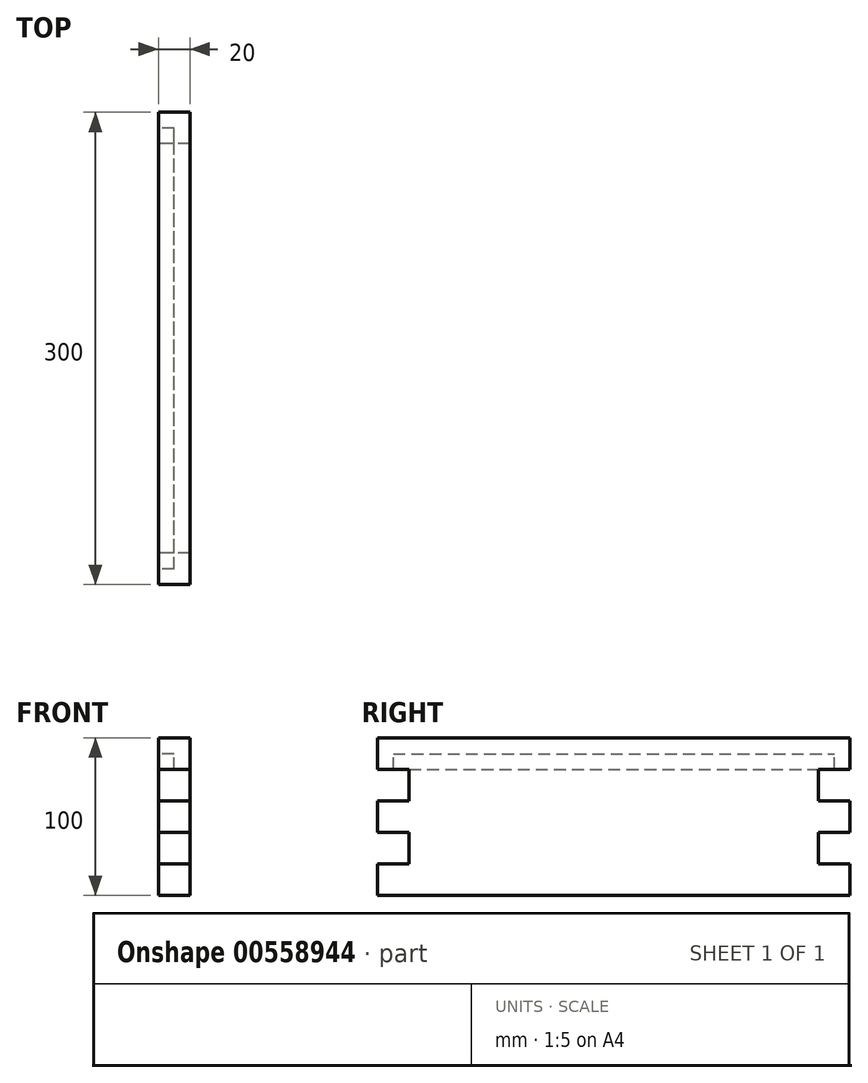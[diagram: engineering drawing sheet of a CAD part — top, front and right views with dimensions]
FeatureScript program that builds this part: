
annotation { "Feature Type Name" : "Feature", "Feature Type Description" : "" }
export const myFeature = defineFeature(function(context is Context, id is Id, definition is map)
    precondition{}
    {
        {
            var Q0;
            Q0=qCreatedBy(makeId("Right.planeOp"),FACE);
            var sketch = newSketch(context, id + "F0", { "sketchPlane" : qUnion([Q0])});
            skLineSegment(sketch, "E0.bottom", {"start": v(150, -50) * mm, "end": v(-150, -50) * mm});
            skLineSegment(sketch, "E0.top", {"start": v(150, 50) * mm, "end": v(-150, 50) * mm});
            skLineSegment(sketch, "E0.left", {"start": v(150, -50) * mm, "end": v(150, 50) * mm});
            skLineSegment(sketch, "E0.right", {"start": v(-150, -50) * mm, "end": v(-150, 50) * mm});
            skPoint(sketch, "E0.middle", {"position": v(0, 0) * mm});
            skSolve(sketch);
        }
        {
            var Q0;
            Q0=makeQuery(id+"F0.imprint","IMPRINT",FACE,{"disambiguationData":[TD([[makeQuery(id+"F0.imprint","IMPRINT",EDGE,{"derivedFrom":sQuery(id+"F0.wireOp",EDGE,"E0.bottom")}),-1.0]])]});
            extrude(context, id + "F1", {"entities" : qUnion([Q0]), "depth" : 20 * mm, "offsetDistance" : 25 * mm});
        }
        {
            var Q0;
            Q0=makeQuery(id+"F1.opExtrude","CAP_FACE",FACE,{"disambiguationData":[OSD([sQuery(id+"F0.wireOp",EDGE,"E0.bottom"),sQuery(id+"F0.wireOp",EDGE,"E0.top"),sQuery(id+"F0.wireOp",EDGE,"E0.left"),sQuery(id+"F0.wireOp",EDGE,"E0.right")])],"isStart":true});
            var sketch = newSketch(context, id + "F2", { "sketchPlane" : qUnion([Q0])});
            skLineSegment(sketch, "E1.bottom", {"start": v(150, -30) * mm, "end": v(130, -30) * mm});
            skLineSegment(sketch, "E1.top", {"start": v(150, -10) * mm, "end": v(130, -10) * mm});
            skLineSegment(sketch, "E1.left", {"start": v(150, -30) * mm, "end": v(150, -10) * mm});
            skLineSegment(sketch, "E1.right", {"start": v(130, -30) * mm, "end": v(130, -10) * mm});
            skLineSegment(sketch, "E2.MirrorCS", {"start": v(-130, -30) * mm, "end": v(-130, -10) * mm});
            skLineSegment(sketch, "E3.MirrorCS", {"start": v(-150, -30) * mm, "end": v(-150, -10) * mm});
            skLineSegment(sketch, "E4.MirrorCS", {"start": v(-150, -10) * mm, "end": v(-130, -10) * mm});
            skLineSegment(sketch, "E5.MirrorCS", {"start": v(-150, -30) * mm, "end": v(-130, -30) * mm});
            skLineSegment(sketch, "E6.bottom", {"start": v(150, 10) * mm, "end": v(130, 10) * mm});
            skLineSegment(sketch, "E6.top", {"start": v(150, 30) * mm, "end": v(130, 30) * mm});
            skLineSegment(sketch, "E6.left", {"start": v(150, 10) * mm, "end": v(150, 30) * mm});
            skLineSegment(sketch, "E6.right", {"start": v(130, 10) * mm, "end": v(130, 30) * mm});
            skLineSegment(sketch, "E7.MirrorCS", {"start": v(-150, 10) * mm, "end": v(-150, 30) * mm});
            skLineSegment(sketch, "E8.MirrorCS", {"start": v(-130, 10) * mm, "end": v(-130, 30) * mm});
            skLineSegment(sketch, "E9.MirrorCS", {"start": v(-150, 10) * mm, "end": v(-130, 10) * mm});
            skLineSegment(sketch, "E10.MirrorCS", {"start": v(-150, 30) * mm, "end": v(-130, 30) * mm});
            skSolve(sketch);
        }
        {
            var Q0;
            Q0=qSketchRegion(id+"F2",true);
            extrude(context, id + "F3", {"entities" : qUnion([Q0]), "operationType" : NewBodyOperationType.REMOVE, "endBound" : BoundingType.UP_TO_NEXT, "oppositeDirection" : true, "depth" : 25 * mm, "offsetDistance" : 25 * mm});
        }
        {
            var Q0;
            Q0=makeQuery(id+"F1.opExtrude","CAP_FACE",FACE,{"disambiguationData":[OSD([sQuery(id+"F0.wireOp",EDGE,"E0.bottom"),sQuery(id+"F0.wireOp",EDGE,"E0.top"),sQuery(id+"F0.wireOp",EDGE,"E0.left"),sQuery(id+"F0.wireOp",EDGE,"E0.right")])],"isStart":true});
            var sketch = newSketch(context, id + "F4", { "sketchPlane" : qUnion([Q0])});
            skLineSegment(sketch, "E11.bottom", {"start": v(140, 30) * mm, "end": v(-140, 30) * mm});
            skLineSegment(sketch, "E11.top", {"start": v(140, 40) * mm, "end": v(-140, 40) * mm});
            skLineSegment(sketch, "E11.left", {"start": v(140, 30) * mm, "end": v(140, 40) * mm});
            skLineSegment(sketch, "E11.right", {"start": v(-140, 30) * mm, "end": v(-140, 40) * mm});
            skPoint(sketch, "E11.middle", {"position": v(0, 35) * mm});
            skSolve(sketch);
        }
        {
            var Q0;
            Q0 = qSketchRegion(id + "F4", true);
            extrude(context, id + "F5", {"entities" : qUnion([Q0]), "operationType" : NewBodyOperationType.REMOVE, "oppositeDirection" : true, "depth" : 10 * mm, "offsetDistance" : 25 * mm});
        }
    });
